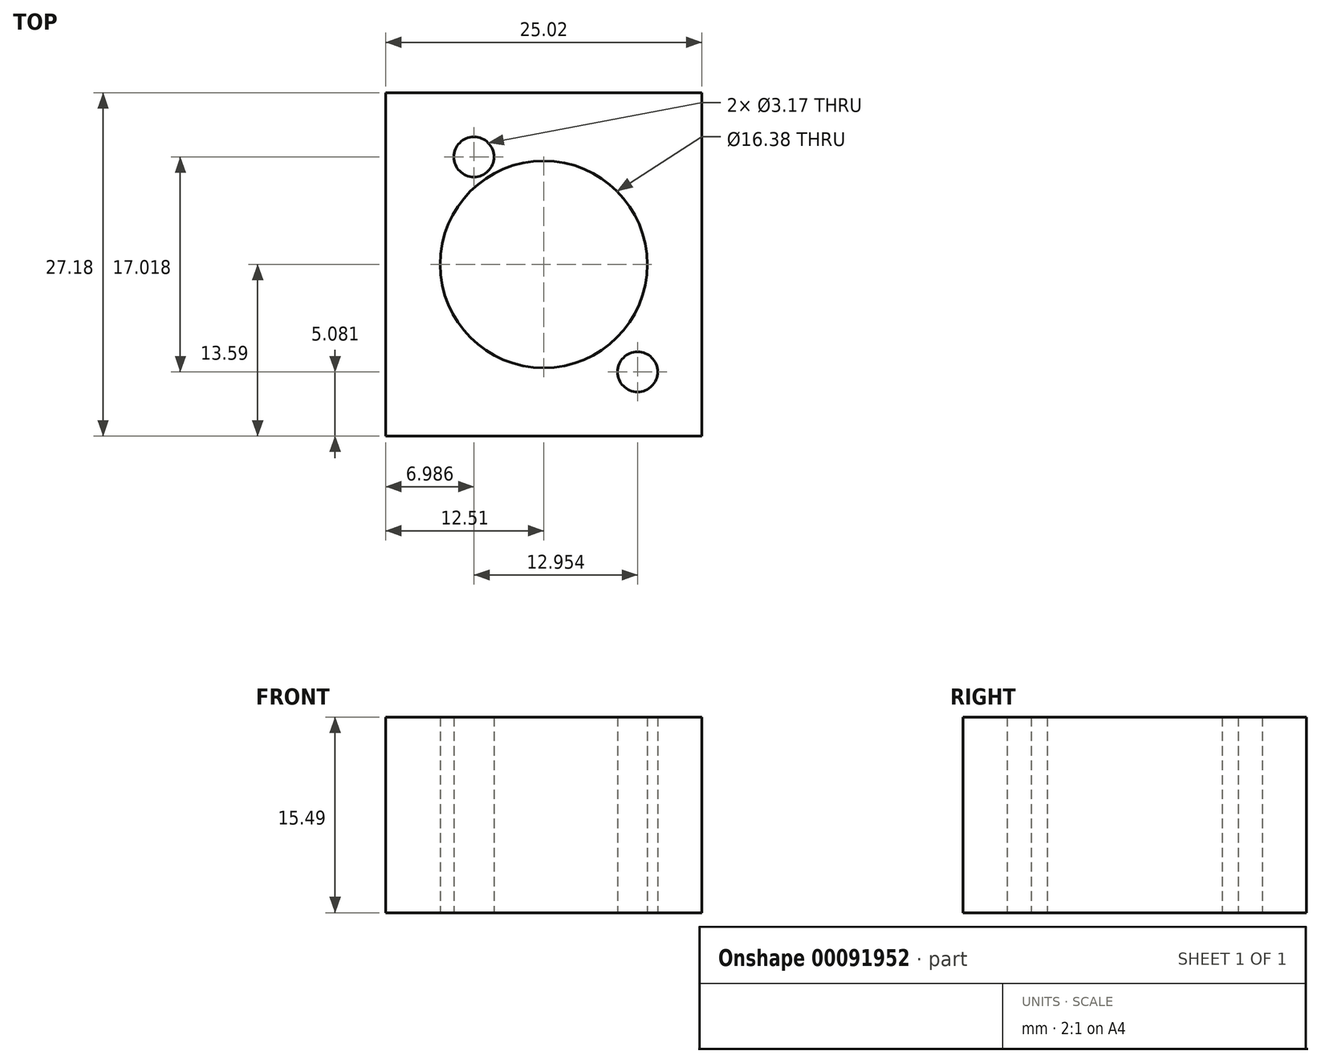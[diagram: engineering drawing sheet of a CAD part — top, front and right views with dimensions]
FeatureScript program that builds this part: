
annotation { "Feature Type Name" : "Feature", "Feature Type Description" : "" }
export const myFeature = defineFeature(function(context is Context, id is Id, definition is map)
    precondition{}
    {
        {
            var Q0;
            Q0=qCreatedBy(makeId("Top.planeOp"),FACE);
            var sketch = newSketch(context, id + "F0", { "sketchPlane" : qUnion([Q0])});
            skLineSegment(sketch, "E0.bottom", {"start": v(-9.97, 11.05) * mm, "end": v(9.97, 11.05) * mm});
            skLineSegment(sketch, "E0.top", {"start": v(-9.97, -11.05) * mm, "end": v(9.97, -11.05) * mm});
            skLineSegment(sketch, "E0.left", {"start": v(-9.97, 11.05) * mm, "end": v(-9.97, -11.05) * mm});
            skLineSegment(sketch, "E0.right", {"start": v(9.97, 11.05) * mm, "end": v(9.97, -11.05) * mm});
            skPoint(sketch, "E0.middle", {"position": v(0, 0) * mm});
            skCircle(sketch, "E1", {"center": v(0, 0) * mm, "radius": 8.2 * mm});
            skCircle(sketch, "E2", {"center": v(-5.52, 8.5) * mm, "radius": 1.59 * mm});
            skCircle(sketch, "E3", {"center": v(7.43, -8.5) * mm, "radius": 1.59 * mm});
            skLineSegment(sketch, "E4.0", {"start": v(-12.5, 13.59) * mm, "end": v(12.5, 13.59) * mm});
            skLineSegment(sketch, "E4.1", {"start": v(-12.5, 13.59) * mm, "end": v(-12.5, -13.59) * mm});
            skLineSegment(sketch, "E4.2", {"start": v(-12.5, -13.59) * mm, "end": v(12.5, -13.59) * mm});
            skLineSegment(sketch, "E4.3", {"start": v(12.5, 13.59) * mm, "end": v(12.5, -13.59) * mm});
            skSolve(sketch);
        }
        {
            var Q0;
            Q0=makeQuery(id+"F0.imprint","IMPRINT",FACE,{"disambiguationData":[TD([[makeQuery(id+"F0.imprint","IMPRINT",EDGE,{"derivedFrom":sQuery(id+"F0.wireOp",EDGE,"E0.bottom")}),-1.0]])]});
            var Q1;
            Q1=makeQuery(id+"F0.imprint","IMPRINT",FACE,{"disambiguationData":[TD([[makeQuery(id+"F0.imprint","IMPRINT",EDGE,{"derivedFrom":sQuery(id+"F0.wireOp",EDGE,"E0.bottom")}),1.0]])]});
            extrude(context, id + "F1", {"entities" : qUnion([Q0, Q1]), "depth" : 15.5 * mm});
        }
    });
